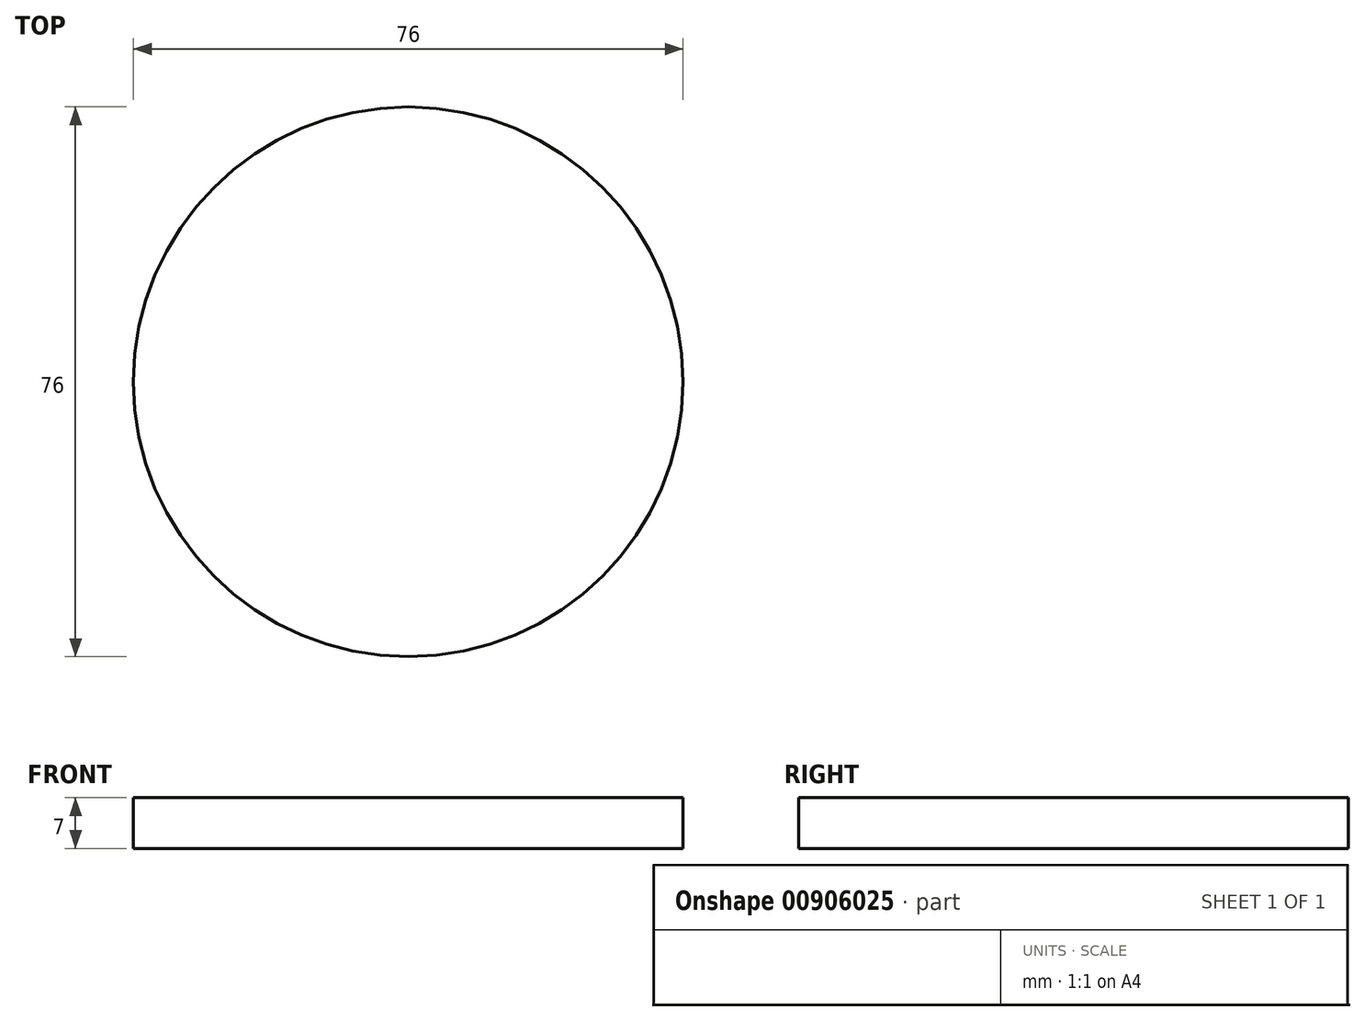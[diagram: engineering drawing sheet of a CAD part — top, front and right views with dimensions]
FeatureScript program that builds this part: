
annotation { "Feature Type Name" : "Feature", "Feature Type Description" : "" }
export const myFeature = defineFeature(function(context is Context, id is Id, definition is map)
    precondition{}
    {
        {
            var Q0;
            Q0=qCreatedBy(makeId("Top.planeOp"),FACE);
            var sketch = newSketch(context, id + "F0", { "sketchPlane" : qUnion([Q0])});
            skCircle(sketch, "E0", {"center": v(0, 0) * mm, "radius": 38 * mm});
            skSolve(sketch);
        }
        {
            var Q0;
            Q0 = qSketchRegion(id + "F0", true);
            extrude(context, id + "F1", {"entities" : qUnion([Q0]), "oppositeDirection" : true, "depth" : 7 * mm, "offsetDistance" : 25 * mm});
        }
    });
